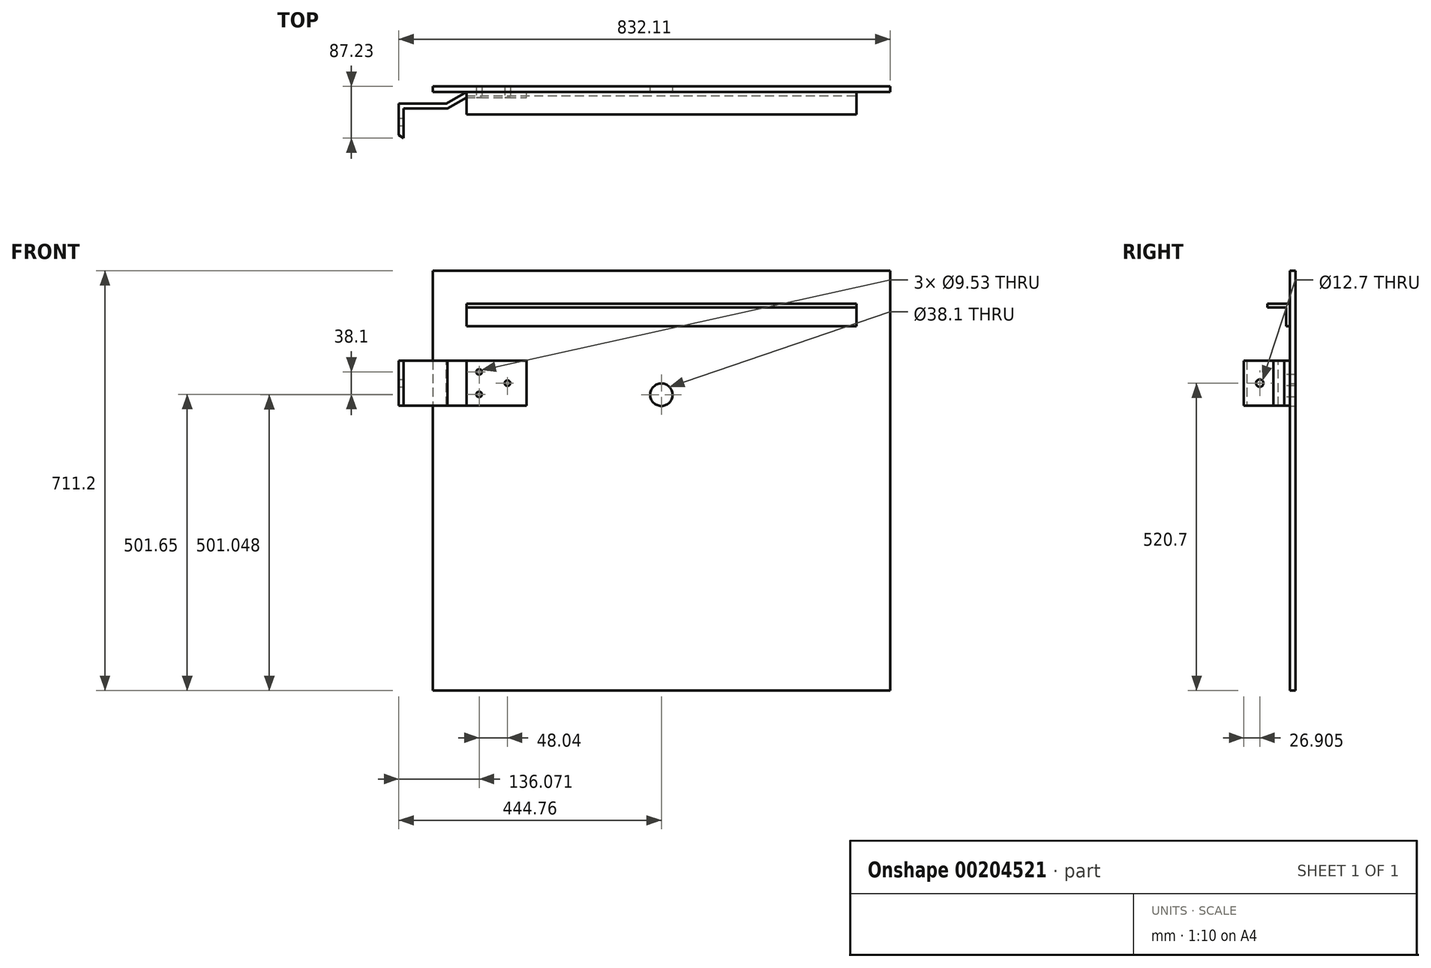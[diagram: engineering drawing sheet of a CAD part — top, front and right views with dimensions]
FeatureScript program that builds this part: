
annotation { "Feature Type Name" : "Feature", "Feature Type Description" : "" }
export const myFeature = defineFeature(function(context is Context, id is Id, definition is map)
    precondition{}
    {
        {
            var Q0;
            Q0=qCreatedBy(makeId("Front.planeOp"),FACE);
            var sketch = newSketch(context, id + "F0", { "sketchPlane" : qUnion([Q0])});
            skLineSegment(sketch, "E0", {"start": v(-387.35, 355.6) * mm, "end": v(-387.35, -355.6) * mm});
            skLineSegment(sketch, "E1", {"start": v(-387.35, -355.6) * mm, "end": v(387.35, -355.6) * mm});
            skLineSegment(sketch, "E2", {"start": v(387.35, -355.6) * mm, "end": v(387.35, 355.6) * mm});
            skLineSegment(sketch, "E3", {"start": v(-387.35, 355.6) * mm, "end": v(387.35, 355.6) * mm});
            skCircle(sketch, "E4", {"center": v(0, 145.45) * mm, "radius": 19.05 * mm});
            skSolve(sketch);
        }
        {
            var Q0;
            Q0=makeQuery(id+"F0.imprint","IMPRINT",FACE,{"disambiguationData":[TD([[makeQuery(id+"F0.imprint","IMPRINT",EDGE,{"derivedFrom":sQuery(id+"F0.wireOp",EDGE,"E0")}),1.0]])]});
            extrude(context, id + "F1", {"entities" : qUnion([Q0]), "depth" : 9.52 * mm});
        }
        {
            var Q0;
            Q0=makeQuery(id+"F1.opExtrude","CAP_FACE",FACE,{"disambiguationData":[OSD([sQuery(id+"F0.wireOp",EDGE,"E0"),sQuery(id+"F0.wireOp",EDGE,"E1"),sQuery(id+"F0.wireOp",EDGE,"E2"),sQuery(id+"F0.wireOp",EDGE,"E3"),sQuery(id+"F0.wireOp",EDGE,"E4")])],"isStart":false});
            var sketch = newSketch(context, id + "F2", { "sketchPlane" : qUnion([Q0])});
            skLineSegment(sketch, "E5", {"start": v(-330.2, 299.4) * mm, "end": v(-330.2, 261.3) * mm});
            skLineSegment(sketch, "E6", {"start": v(-330.2, 261.3) * mm, "end": v(330.2, 261.3) * mm});
            skLineSegment(sketch, "E7", {"start": v(330.2, 261.3) * mm, "end": v(330.2, 299.4) * mm});
            skLineSegment(sketch, "E8", {"start": v(-330.2, 299.4) * mm, "end": v(330.2, 299.4) * mm});
            skLineSegment(sketch, "E9.0", {"start": v(-330.2, 293.05) * mm, "end": v(330.2, 293.05) * mm});
            skLineSegment(sketch, "E10", {"start": v(-330.2, 203.2) * mm, "end": v(-228.6, 203.2) * mm});
            skLineSegment(sketch, "E11", {"start": v(-228.6, 203.2) * mm, "end": v(-228.6, 127) * mm});
            skLineSegment(sketch, "E12", {"start": v(-228.6, 127) * mm, "end": v(-330.2, 127) * mm});
            skLineSegment(sketch, "E13", {"start": v(-330.2, 203.2) * mm, "end": v(-330.2, 127) * mm});
            skSolve(sketch);
        }
        {
            var Q0;
            {var subQ0=sQuery(id+"F2.wireOp",EDGE,"E8");Q0=makeQuery(id+"F2.imprint","IMPRINT",FACE,{"disambiguationData":[TD([[makeQuery(id+"F2.imprint","IMPRINT",EDGE,{"derivedFrom":subQ0}),-1.0]])]});}
            extrude(context, id + "F3", {"entities" : qUnion([Q0]), "operationType" : NewBodyOperationType.ADD, "depth" : 38.1 * mm});
        }
        {
            var Q0;
            {var subQ0=sQuery(id+"F2.wireOp",EDGE,"E6");Q0=makeQuery(id+"F2.imprint","IMPRINT",FACE,{"disambiguationData":[TD([[makeQuery(id+"F2.imprint","IMPRINT",EDGE,{"derivedFrom":subQ0}),1.0]])]});}
            extrude(context, id + "F4", {"entities" : qUnion([Q0]), "operationType" : NewBodyOperationType.ADD, "depth" : 6.35 * mm});
        }
        {
            var Q0;
            Q0=makeQuery(id+"F2.imprint","IMPRINT",FACE,{"disambiguationData":[TD([[makeQuery(id+"F2.imprint","IMPRINT",EDGE,{"derivedFrom":sQuery(id+"F2.wireOp",EDGE,"E10")}),-1.0]])]});
            extrude(context, id + "F5", {"entities" : qUnion([Q0]), "operationType" : NewBodyOperationType.ADD, "depth" : 9.52 * mm});
        }
        {
            var Q0;
            Q0=qCreatedBy(makeId("Top.planeOp"),FACE);
            var sketch = newSketch(context, id + "F6", { "sketchPlane" : qUnion([Q0])});
            skLineSegment(sketch, "E14", {"start": v(-329.77, -15.97) * mm, "end": v(-362.76, -35.02) * mm});
            skLineSegment(sketch, "E15", {"start": v(-362.76, -35.02) * mm, "end": v(-438.96, -35.02) * mm});
            skLineSegment(sketch, "E16", {"start": v(-438.96, -35.02) * mm, "end": v(-438.96, -85.82) * mm});
            skSolve(sketch);
        }
        {
            var Q0;
            Q0=makeQuery(id+"F5.opExtrude","SWEPT_FACE",FACE,{"disambiguationData":[OSD([sQuery(id+"F2.wireOp",EDGE,"E13")])]});
            var Q1;
            Q1=sQuery(id+"F6.wireOp",EDGE,"E14");
            var Q2;
            Q2=sQuery(id+"F6.wireOp",EDGE,"E15");
            var Q3;
            Q3=sQuery(id+"F6.wireOp",EDGE,"E16");
            sweep(context, id + "F7", {"operationType" : NewBodyOperationType.ADD, "profiles" : qUnion([Q0]), "path" : qUnion([Q1, Q2, Q3])});
        }
        {
            var Q0;
            {var subQ0=sQuery(id+"F6.wireOp",EDGE,"E16");var subQ1=sQuery(id+"F2.wireOp",EDGE,"E13");Q0=makeQuery(id+"F7.opSweep","SWEPT_FACE",FACE,{"disambiguationData":[OSD([subQ1,subQ0]),TDD([makeQuery(id+"F5.opExtrude","CAP_EDGE",EDGE,{"disambiguationData":[OSD([subQ1])],"isStart":false}),subQ0])]});}
            var sketch = newSketch(context, id + "F8", { "sketchPlane" : qUnion([Q0])});
            skLineSegment(sketch, "E17", {"start": v(-87.73, 165.1) * mm, "end": v(-60.33, 165.1) * mm});
            skPoint(sketch, "E17.endSnap0", {"position": v(-60.32, 127) * mm});
            skSolve(sketch);
        }
        {
            var Q0;
            Q0=sQuery(id+"F8.wireOp",VERTEX,"E17.end");
            var Q1;
            Q1=makeQuery(id+"F1.opExtrude","SWEPT_BODY",BODY,{"disambiguationData":[OSD([sQuery(id+"F0.wireOp",EDGE,"E0"),sQuery(id+"F0.wireOp",EDGE,"E1"),sQuery(id+"F0.wireOp",EDGE,"E2"),sQuery(id+"F0.wireOp",EDGE,"E3"),sQuery(id+"F0.wireOp",EDGE,"E4")])]});
            hole(context, id + "F9", {"style" : HoleStyle.SIMPLE, "endStyle" : HoleEndStyle.BLIND, "holeDiameter" : 12.7 * mm, "holeDepth" : 127 * mm, "locations" : qUnion([Q0]), "scope" : qUnion([Q1])});
        }
        {
            var Q0;
            Q0=makeQuery(id+"F5.opExtrude","CAP_FACE",FACE,{"disambiguationData":[OSD([sQuery(id+"F2.wireOp",EDGE,"E10"),sQuery(id+"F2.wireOp",EDGE,"E11"),sQuery(id+"F2.wireOp",EDGE,"E12"),sQuery(id+"F2.wireOp",EDGE,"E13")])],"isStart":false});
            var sketch = newSketch(context, id + "F10", { "sketchPlane" : qUnion([Q0])});
            skLineSegment(sketch, "E18", {"start": v(-228.6, 165.1) * mm, "end": v(-330.2, 203.2) * mm});
            skLineSegment(sketch, "E19", {"start": v(-228.6, 165.1) * mm, "end": v(-330.2, 127) * mm});
            skCircle(sketch, "E20", {"center": v(-308.69, 184.15) * mm, "radius": 5.47 * mm});
            skPoint(sketch, "E20.centerSnap0", {"position": v(-279.4, 184.15) * mm});
            skLineSegment(sketch, "E21", {"start": v(-228.6, 165.1) * mm, "end": v(-330.2, 165.1) * mm});
            skCircle(sketch, "E22", {"center": v(-260.65, 165.1) * mm, "radius": 11.25 * mm});
            skCircle(sketch, "E23.MirrorC", {"center": v(-308.69, 146.05) * mm, "radius": 5.47 * mm});
            skSolve(sketch);
        }
        {
            var Q0;
            Q0=sQuery(id+"F10.wireOp",VERTEX,"E20.center");
            var Q1;
            Q1=sQuery(id+"F10.wireOp",VERTEX,"E23.MirrorC.center");
            var Q2;
            Q2=sQuery(id+"F10.wireOp",VERTEX,"E22.center");
            var Q3;
            Q3=makeQuery(id+"F1.opExtrude","SWEPT_BODY",BODY,{"disambiguationData":[OSD([sQuery(id+"F0.wireOp",EDGE,"E0"),sQuery(id+"F0.wireOp",EDGE,"E1"),sQuery(id+"F0.wireOp",EDGE,"E2"),sQuery(id+"F0.wireOp",EDGE,"E3"),sQuery(id+"F0.wireOp",EDGE,"E4")])]});
            hole(context, id + "F11", {"style" : HoleStyle.SIMPLE, "endStyle" : HoleEndStyle.BLIND, "holeDiameter" : 9.52 * mm, "holeDepth" : 50.8 * mm, "locations" : qUnion([Q0, Q1, Q2]), "scope" : qUnion([Q3])});
        }
    });
